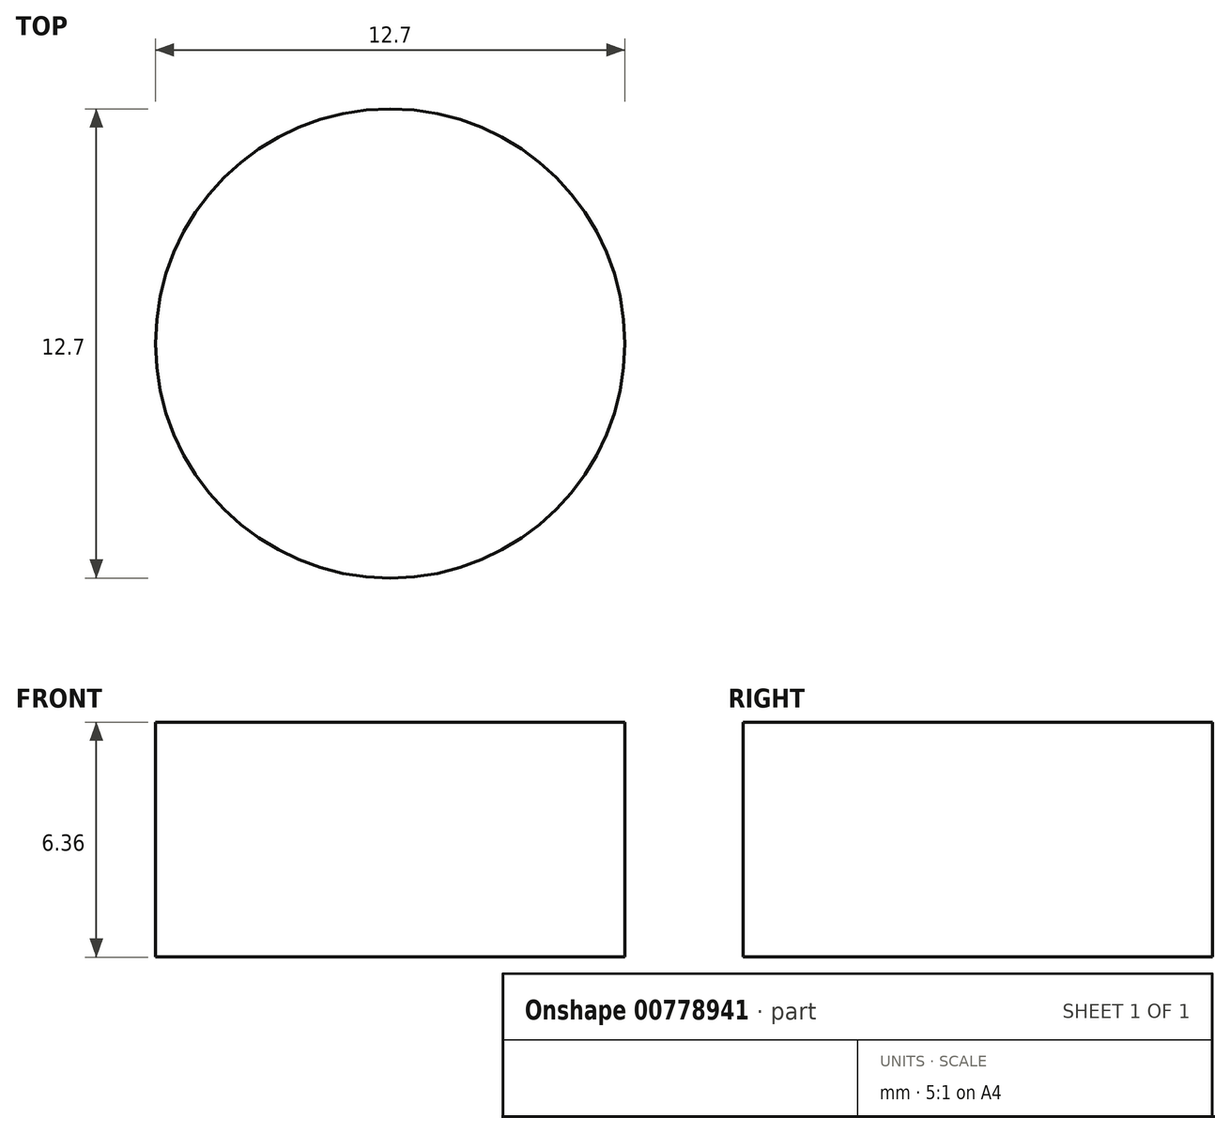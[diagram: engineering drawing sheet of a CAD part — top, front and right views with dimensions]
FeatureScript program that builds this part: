
annotation { "Feature Type Name" : "Feature", "Feature Type Description" : "" }
export const myFeature = defineFeature(function(context is Context, id is Id, definition is map)
    precondition{}
    {
        {
            var Q0;
            Q0=qCreatedBy(makeId("Top.planeOp"),FACE);
            var sketch = newSketch(context, id + "F0", { "sketchPlane" : qUnion([Q0])});
            skCircle(sketch, "E0", {"center": v(0, 0) * mm, "radius": 6.35 * mm});
            skSolve(sketch);
        }
        {
            var Q0;
            Q0 = qSketchRegion(id + "F0", true);
            extrude(context, id + "F1", {"entities" : qUnion([Q0]), "endBound" : BoundingType.SYMMETRIC, "depth" : 6.35 * mm, "offsetDistance" : 25.4 * mm});
        }
    });
